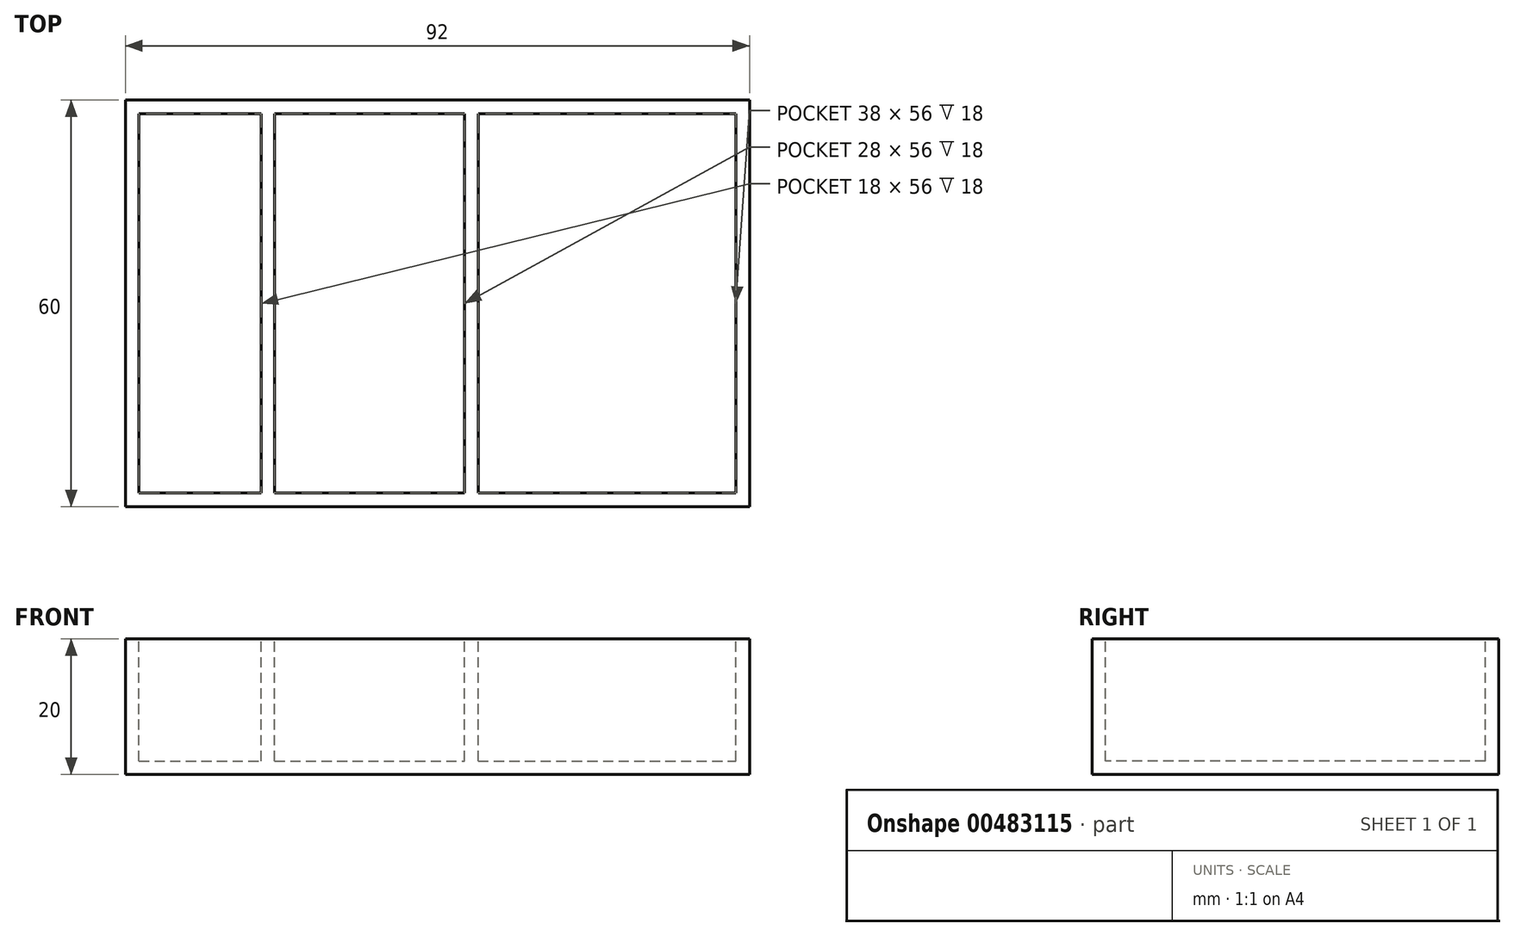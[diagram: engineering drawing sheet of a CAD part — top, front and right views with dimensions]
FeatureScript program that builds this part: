
annotation { "Feature Type Name" : "Feature", "Feature Type Description" : "" }
export const myFeature = defineFeature(function(context is Context, id is Id, definition is map)
    precondition{}
    {
        {
            var Q0;
            Q0=qCreatedBy(makeId("Top.planeOp"),FACE);
            var sketch = newSketch(context, id + "F0", { "sketchPlane" : qUnion([Q0])});
            skLineSegment(sketch, "E0.bottom", {"start": v(46, -30) * mm, "end": v(-46, -30) * mm});
            skLineSegment(sketch, "E0.top", {"start": v(46, 30) * mm, "end": v(-46, 30) * mm});
            skLineSegment(sketch, "E0.left", {"start": v(46, -30) * mm, "end": v(46, 30) * mm});
            skLineSegment(sketch, "E0.right", {"start": v(-46, -30) * mm, "end": v(-46, 30) * mm});
            skPoint(sketch, "E0.middle", {"position": v(0, 0) * mm});
            skSolve(sketch);
        }
        {
            var Q0;
            Q0 = qSketchRegion(id + "F0", true);
            extrude(context, id + "F1", {"entities" : qUnion([Q0]), "depth" : 20 * mm});
        }
        {
            var Q0;
            Q0=makeQuery(id+"F1.opExtrude","CAP_FACE",FACE,{"disambiguationData":[OSD([sQuery(id+"F0.wireOp",EDGE,"E0.bottom"),sQuery(id+"F0.wireOp",EDGE,"E0.top"),sQuery(id+"F0.wireOp",EDGE,"E0.left"),sQuery(id+"F0.wireOp",EDGE,"E0.right")])],"isStart":false});
            var sketch = newSketch(context, id + "F2", { "sketchPlane" : qUnion([Q0])});
            skLineSegment(sketch, "E1.bottom", {"start": v(-44, 28) * mm, "end": v(-26, 28) * mm});
            skLineSegment(sketch, "E1.top", {"start": v(-44, -28) * mm, "end": v(-26, -28) * mm});
            skLineSegment(sketch, "E1.left", {"start": v(-44, 28) * mm, "end": v(-44, -28) * mm});
            skLineSegment(sketch, "E1.right", {"start": v(-26, 28) * mm, "end": v(-26, -28) * mm});
            skLineSegment(sketch, "E2.bottom", {"start": v(-24, 28) * mm, "end": v(4, 28) * mm});
            skLineSegment(sketch, "E2.top", {"start": v(-24, -28) * mm, "end": v(4, -28) * mm});
            skLineSegment(sketch, "E2.left", {"start": v(-24, 28) * mm, "end": v(-24, -28) * mm});
            skLineSegment(sketch, "E2.right", {"start": v(4, 28) * mm, "end": v(4, -28) * mm});
            skLineSegment(sketch, "E3.bottom", {"start": v(6, 28) * mm, "end": v(44, 28) * mm});
            skLineSegment(sketch, "E3.top", {"start": v(6, -28) * mm, "end": v(44, -28) * mm});
            skLineSegment(sketch, "E3.left", {"start": v(6, 28) * mm, "end": v(6, -28) * mm});
            skLineSegment(sketch, "E3.right", {"start": v(44, 28) * mm, "end": v(44, -28) * mm});
            skSolve(sketch);
        }
        {
            var Q0;
            Q0=makeQuery(id+"F2.imprint","IMPRINT",FACE,{"disambiguationData":[TD([[makeQuery(id+"F2.imprint","IMPRINT",EDGE,{"derivedFrom":sQuery(id+"F2.wireOp",EDGE,"E1.bottom")}),-1.0]])]});
            var Q1;
            Q1=makeQuery(id+"F2.imprint","IMPRINT",FACE,{"disambiguationData":[TD([[makeQuery(id+"F2.imprint","IMPRINT",EDGE,{"derivedFrom":sQuery(id+"F2.wireOp",EDGE,"E2.bottom")}),-1.0]])]});
            var Q2;
            Q2=makeQuery(id+"F2.imprint","IMPRINT",FACE,{"disambiguationData":[TD([[makeQuery(id+"F2.imprint","IMPRINT",EDGE,{"derivedFrom":sQuery(id+"F2.wireOp",EDGE,"E3.bottom")}),-1.0]])]});
            extrude(context, id + "F3", {"entities" : qUnion([Q0, Q1, Q2]), "operationType" : NewBodyOperationType.REMOVE, "oppositeDirection" : true, "depth" : 18 * mm});
        }
    });
